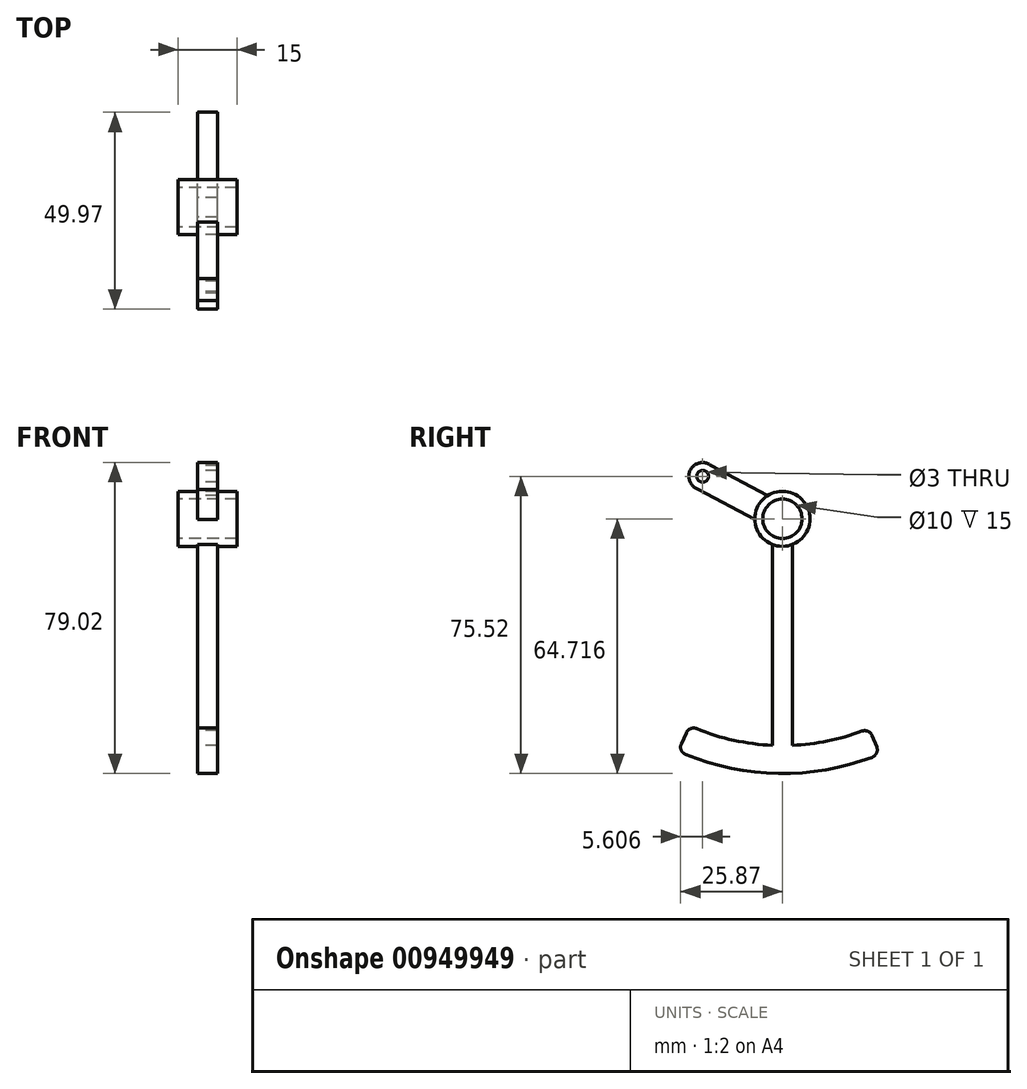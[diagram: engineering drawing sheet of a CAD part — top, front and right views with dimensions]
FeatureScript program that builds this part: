
annotation { "Feature Type Name" : "Feature", "Feature Type Description" : "" }
export const myFeature = defineFeature(function(context is Context, id is Id, definition is map)
    precondition{}
    {
        {
            var Q0;
            Q0=qCreatedBy(makeId("Right.planeOp"),FACE);
            var sketch = newSketch(context, id + "F0", { "sketchPlane" : qUnion([Q0])});
            skLineSegment(sketch, "E0", {"start": v(0, -22.45) * mm, "end": v(0, 63.25) * mm, "construction": true});
            skLineSegment(sketch, "E1", {"start": v(0, 63.25) * mm, "end": v(-66.16, 65.6) * mm, "construction": true});
            skCircle(sketch, "E2", {"center": v(0, 63.25) * mm, "radius": 5 * mm});
            skCircle(sketch, "E3", {"center": v(0, 63.25) * mm, "radius": 7 * mm});
            skLineSegment(sketch, "E4", {"start": v(-2.5, 56.7) * mm, "end": v(-2.5, 5.69) * mm});
            skLineSegment(sketch, "E5", {"start": v(2.5, 5.69) * mm, "end": v(2.5, 56.7) * mm});
            skLineSegment(sketch, "E6", {"start": v(2.5, 56.7) * mm, "end": v(-2.5, 56.7) * mm});
            skLineSegment(sketch, "E7", {"start": v(0, 63.25) * mm, "end": v(-36.27, 82.58) * mm, "construction": true});
            skCircle(sketch, "E8", {"center": v(-20.26, 74.05) * mm, "radius": 3.5 * mm});
            skCircle(sketch, "E9", {"center": v(-20.26, 74.05) * mm, "radius": 1.5 * mm});
            skLineSegment(sketch, "E10", {"start": v(-3.75, 69.16) * mm, "end": v(-18.14, 76.83) * mm});
            skPoint(sketch, "E10.endSnap0", {"position": v(-18.14, 72.92) * mm});
            skLineSegment(sketch, "E11", {"start": v(-18.14, 76.83) * mm, "end": v(-21.38, 70.73) * mm});
            skLineSegment(sketch, "E12", {"start": v(-21.38, 70.73) * mm, "end": v(-7, 63.06) * mm});
            skArc(sketch, "E13", {"start": v(-21.84, 9.94) * mm, "mid": v(-0.87, 5.64) * mm, "end": v(20.22, 9.3) * mm});
            skArc(sketch, "E14", {"start": v(-24.63, 3.4) * mm, "mid": v(-0.98, -1.46) * mm, "end": v(22.8, 2.69) * mm});
            skLineSegment(sketch, "E15", {"start": v(0, 63.25) * mm, "end": v(-2.87, 56.86) * mm});
            skLineSegment(sketch, "E16", {"start": v(0, 63.25) * mm, "end": v(2.67, 56.78) * mm});
            skLineSegment(sketch, "E17.trimOffspring", {"start": v(-24.42, 8.9) * mm, "end": v(-25.7, 6.07) * mm});
            skLineSegment(sketch, "E18.trimOffspring", {"start": v(22.77, 8.2) * mm, "end": v(23.95, 5.32) * mm});
            skPoint(sketch, "E19.visualSharp", {"position": v(-26.53, 4.22) * mm});
            skArc(sketch, "E19.filletArc", {"start": v(-25.7, 6.07) * mm, "mid": v(-25.73, 4.51) * mm, "end": v(-24.63, 3.4) * mm});
            skPoint(sketch, "E20.visualSharp", {"position": v(-23.62, 10.7) * mm});
            skArc(sketch, "E20.filletArc", {"start": v(-21.84, 9.94) * mm, "mid": v(-23.34, 9.94) * mm, "end": v(-24.42, 8.9) * mm});
            skPoint(sketch, "E21.visualSharp", {"position": v(24.73, 3.44) * mm});
            skArc(sketch, "E21.filletArc", {"start": v(22.8, 2.69) * mm, "mid": v(23.94, 3.76) * mm, "end": v(23.95, 5.32) * mm});
            skPoint(sketch, "E22.visualSharp", {"position": v(22.01, 10) * mm});
            skArc(sketch, "E22.filletArc", {"start": v(22.77, 8.2) * mm, "mid": v(21.72, 9.26) * mm, "end": v(20.22, 9.3) * mm});
            skSolve(sketch);
        }
        {
            var Q0;
            Q0 = qSketchRegion(id + "F0", true);
            extrude(context, id + "F1", {"entities" : qUnion([Q0]), "depth" : 5 * mm, "offsetDistance" : 25 * mm});
        }
        {
            var Q0;
            Q0=makeQuery(id+"F0.imprint","IMPRINT",FACE,{"disambiguationData":[TD([[makeQuery(id+"F0.imprint","IMPRINT",EDGE,{"derivedFrom":sQuery(id+"F0.wireOp",EDGE,"E2")}),-1.0]])]});
            var Q1;
            {var subQ0=sQuery(id+"F0.wireOp",EDGE,"E6");Q1=makeQuery(id+"F0.imprint","IMPRINT",FACE,{"disambiguationData":[TD([[makeQuery(id+"F0.imprint","IMPRINT",EDGE,{"derivedFrom":subQ0}),-1.0]])]});}
            var Q2;
            {var subQ0=sQuery(id+"F0.wireOp",EDGE,"E6");Q2=makeQuery(id+"F0.imprint","IMPRINT",FACE,{"disambiguationData":[TD([[makeQuery(id+"F0.imprint","IMPRINT",EDGE,{"derivedFrom":subQ0}),1.0]])]});}
            extrude(context, id + "F2", {"entities" : qUnion([Q0, Q1, Q2]), "operationType" : NewBodyOperationType.ADD, "depth" : 10 * mm, "offsetDistance" : 25 * mm, "hasSecondDirection" : true, "secondDirectionOppositeDirection" : true, "secondDirectionDepth" : 5 * mm});
        }
    });
